FCSTD DOCUMENT  (FreeCAD 1.0R39319 (Git))
Label: Week1Sketch3
License: All rights reserved
LicenseURL: https://en.wikipedia.org/wiki/All_rights_reserved
objects: PartDesign::Body×2, Sketcher::SketchObject×1
note: 4 computed .brp shape members not serialized (recipe doc carries the construction recipe); baked Part::Feature solids carry a one-line shape summary decoded from their .brp

FEATURE [PartDesign::Body] Body
  AllowCompound = false
  Origin = -> Origin
FEATURE [Sketcher::SketchObject] Sketch
  ArcFitTolerance = 1e-06
  AttachmentSupport = -> [XY_Plane001]
  FullyConstrained = true
  MakeInternals = false
  MapMode = 5
  sketch-geometry (23):
    g0: ArcOfCircle CenterX=0 CenterY=0 CenterZ=0 NormalX=0 NormalY=0 NormalZ=1 AngleXU=0 Radius=40 StartAngle=2.23125 EndAngle=7.19353
    g1: ArcOfCircle CenterX=0 CenterY=-18 CenterZ=0 NormalX=0 NormalY=0 NormalZ=1 AngleXU=0 Radius=10 StartAngle=3.21308 EndAngle=6.2117
    g2: ArcOfCircle CenterX=0 CenterY=10 CenterZ=0 NormalX=0 NormalY=0 NormalZ=1 AngleXU=0 Radius=12 StartAngle=6.2117 EndAngle=9.49627
    g3: LineSegment StartX=-11.9693 StartY=9.14286 StartZ=0 EndX=-9.97446 EndY=-18.7143 EndZ=0
    g4: LineSegment StartX=9.97446 StartY=-18.7143 StartZ=0 EndX=11.9693 EndY=9.14286 EndZ=0
    g5: ArcOfCircle CenterX=0 CenterY=128 CenterZ=0 NormalX=0 NormalY=0 NormalZ=1 AngleXU=0 Radius=22 StartAngle=2e-16 EndAngle=3.14159
    g6: ArcOfCircle CenterX=-3e-16 CenterY=100 CenterZ=0 NormalX=0 NormalY=0 NormalZ=1 AngleXU=0 Radius=22 StartAngle=3.14159 EndAngle=6.28319
    g7: LineSegment StartX=22 StartY=128 StartZ=0 EndX=22 EndY=100 EndZ=0
    g8: LineSegment StartX=-22 StartY=128 StartZ=0 EndX=-22 EndY=100 EndZ=0
    g9: ArcOfCircle CenterX=0 CenterY=128 CenterZ=0 NormalX=0 NormalY=0 NormalZ=1 AngleXU=0 Radius=10 StartAngle=6.28309 EndAngle=9.42478
    g10: LineSegment StartX=10 StartY=127.999 StartZ=0 EndX=9.99872 EndY=114 EndZ=0
    g11: LineSegment StartX=-10 StartY=128 StartZ=0 EndX=-10 EndY=114 EndZ=0
    g12: ArcOfCircle CenterX=-3e-16 CenterY=100 CenterZ=0 NormalX=0 NormalY=0 NormalZ=1 AngleXU=0 Radius=12 StartAngle=3.14159 EndAngle=6.28319
    g13: ArcOfCircle CenterX=-9 CenterY=111.172 CenterZ=0 NormalX=0 NormalY=0 NormalZ=1 AngleXU=0 Radius=3 StartAngle=1.91063 EndAngle=3.14159
    g14: LineSegment StartX=-12 StartY=100 StartZ=0 EndX=-12 EndY=111.172 EndZ=0
    g15: ArcOfCircle CenterX=9 CenterY=111.172 CenterZ=0 NormalX=0 NormalY=0 NormalZ=1 AngleXU=0 Radius=3 StartAngle=-1.8e-15 EndAngle=1.23141
    g16: LineSegment StartX=12 StartY=100 StartZ=0 EndX=12 EndY=111.172 EndZ=0
    g17: ArcOfCircle CenterX=-42.9432 CenterY=55.28 CenterZ=0 NormalX=0 NormalY=0 NormalZ=1 AngleXU=0 Radius=30 StartAngle=5.37284 EndAngle=7.08885
    g18: ArcOfCircle CenterX=-3e-16 CenterY=100 CenterZ=0 NormalX=0 NormalY=0 NormalZ=1 AngleXU=0 Radius=32 StartAngle=2.77639 EndAngle=3.94726
    g19: LineSegment StartX=-20.5491 StartY=135.857 StartZ=0 EndX=-29.8896 EndY=111.429 EndZ=0
    g20: ArcOfCircle CenterX=42.9432 CenterY=55.28 CenterZ=0 NormalX=0 NormalY=0 NormalZ=1 AngleXU=0 Radius=30 StartAngle=2.33593 EndAngle=4.05194
    g21: ArcOfCircle CenterX=-1.69e-14 CenterY=100 CenterZ=0 NormalX=0 NormalY=0 NormalZ=1 AngleXU=0 Radius=32 StartAngle=5.47752 EndAngle=6.64839
    g22: LineSegment StartX=20.5491 StartY=135.857 StartZ=0 EndX=29.8896 EndY=111.429 EndZ=0
  constraints (55):
    c: Coincident(g0,g-1)
    c: Diameter(g0) = 80
    c: PointOnObject(g1,g-2)
    c: Diameter(g1) = 20
    c: PointOnObject(g2,g-2)
    c: Diameter(g2) = 24
    c: Distance(g0,g2) = 10
    c: Distance(g1,g2) = 28
    c: Tangent(g1,g4) = -1.5708
    c: Tangent(g1,g3) = -1.5708
    c: Tangent(g2,g3) = -1.5708
    c: Tangent(g2,g4) = -1.5708
    c: Tangent(g5,g7) = 1.5708
    c: Tangent(g5,g8) = -1.5708
    c: Tangent(g6,g7) = 1.5708
    c: Tangent(g6,g8) = -1.5708
    c: Equal(g5,g6)
    c: Vertical(g8)
    c: Distance(g5,g6) = 28
    c: Radius(g5) = 22
    c: PointOnObject(g5,g-2)
    c: DistanceY(g-1,g5) = 128
    c: Tangent(g9,g10) = 1.5708
    c: Tangent(g9,g11) = -1.5708
    c: Vertical(g11)
    c: Radius(g9) = 10
    c: Coincident(g9,g5)
    c: Diameter(g12) = 24
    c: Coincident(g12,g6)
    c: Vertical(g14)
    c: Radius(g13) = 3
    c: DistanceY(g13,g5) = 14
    c: Tangent(g13,g14) = 1.5708
    c: Radius(g15) = 3
    c: Block(g15)
    c: Block(g16)
    c: Coincident(g11,g13)
    c: Tangent(g12,g14) = 1.5708
    c: Coincident(g10,g15)
    c: Coincident(g12,g16)
    c: Tangent(g17,g18) = 1.5708
    c: Coincident(g18,g6)
    c: Radius(g17) = 30
    c: Radius(g18) = 32
    c: Tangent(g19,g18) = -1.5708
    c: Tangent(g19,g5) = -1.5708
    c: Tangent(g20,g21) = 1.5708
    c: Radius(g20) = 30
    c: Radius(g21) = 32
    c: Tangent(g22,g21) = 1.5708
    c: Block(g21)
    c: Block(g20)
    c: Block(g22)
    c: Coincident(g0,g20)
    c: Tangent(g0,g17) = 1.5708
FEATURE [PartDesign::Body] Body001
  AllowCompound = false
  Group = -> [Sketch]
  Origin = -> Origin001
